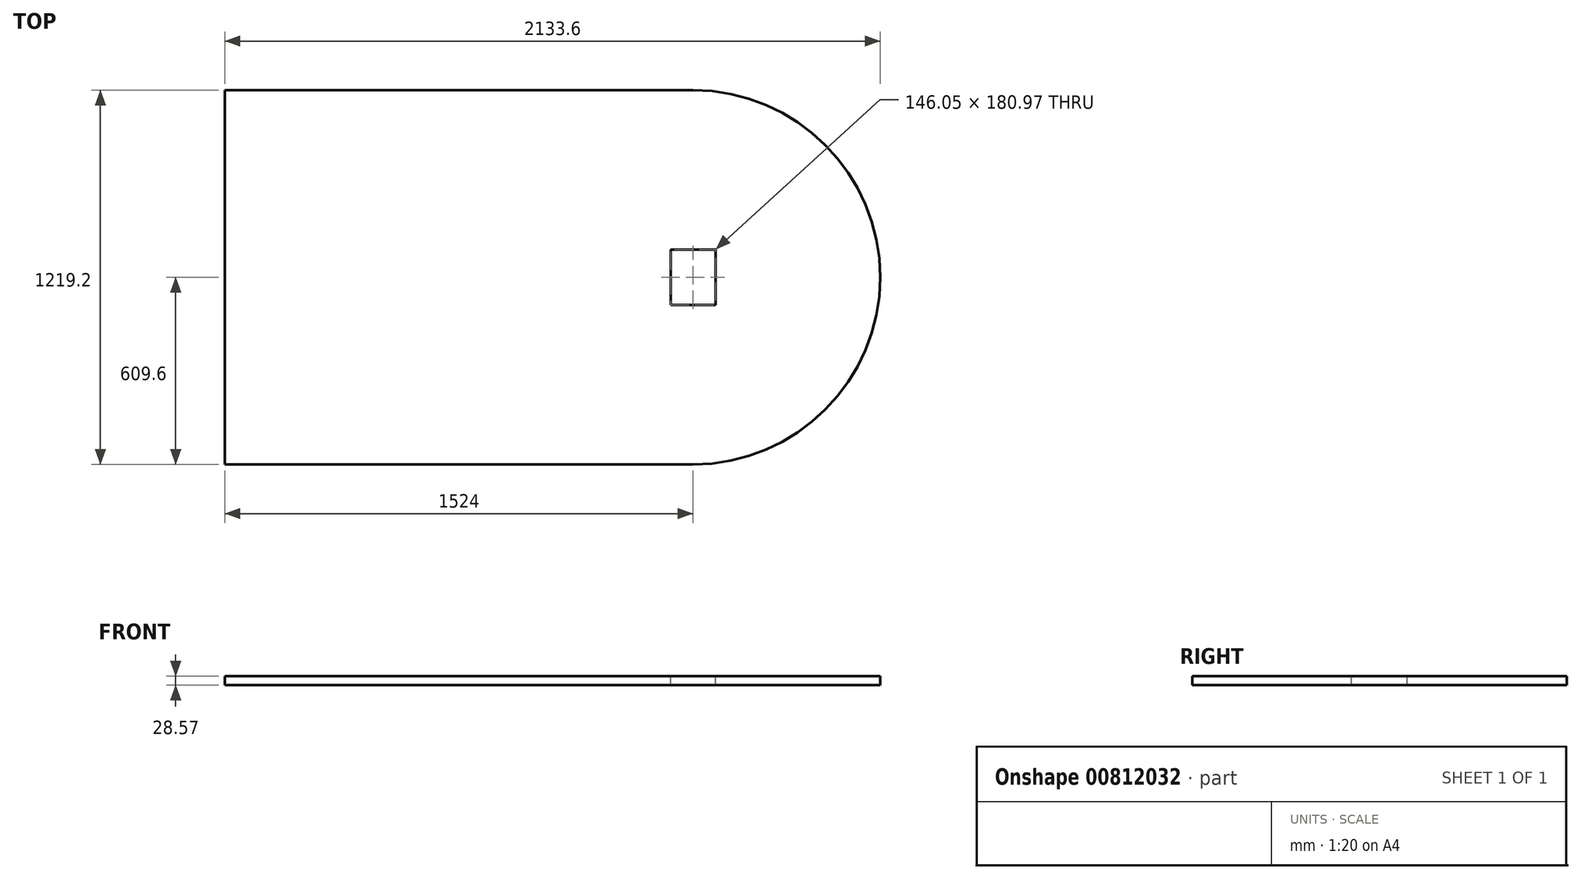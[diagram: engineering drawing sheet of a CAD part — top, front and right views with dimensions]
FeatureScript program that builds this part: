
annotation { "Feature Type Name" : "Feature", "Feature Type Description" : "" }
export const myFeature = defineFeature(function(context is Context, id is Id, definition is map)
    precondition{}
    {
        {
            var Q0;
            Q0=qCreatedBy(makeId("Top.planeOp"),FACE);
            var sketch = newSketch(context, id + "F0", { "sketchPlane" : qUnion([Q0])});
            skLineSegment(sketch, "E0.bottom", {"start": v(-762, 609.6) * mm, "end": v(762, 609.6) * mm});
            skLineSegment(sketch, "E0.top", {"start": v(-762, -609.6) * mm, "end": v(762, -609.6) * mm});
            skLineSegment(sketch, "E0.left", {"start": v(-762, 609.6) * mm, "end": v(-762, -609.6) * mm});
            skLineSegment(sketch, "E0.right", {"start": v(762, 609.6) * mm, "end": v(762, -609.6) * mm});
            skPoint(sketch, "E0.middle", {"position": v(0, 0) * mm});
            skArc(sketch, "E1", {"start": v(762, 609.6) * mm, "mid": v(1371.6, 0) * mm, "end": v(762, -609.6) * mm});
            skSolve(sketch);
        }
        {
            var Q0;
            Q0=makeQuery(id+"F0.imprint","IMPRINT",FACE,{"disambiguationData":[TD([[makeQuery(id+"F0.imprint","IMPRINT",EDGE,{"derivedFrom":sQuery(id+"F0.wireOp",EDGE,"E0.bottom")}),-1.0]])]});
            var Q1;
            Q1=makeQuery(id+"F0.imprint","IMPRINT",FACE,{"disambiguationData":[TD([[makeQuery(id+"F0.imprint","IMPRINT",EDGE,{"derivedFrom":sQuery(id+"F0.wireOp",EDGE,"E0.right")}),1.0]])]});
            extrude(context, id + "F1", {"entities" : qUnion([Q0, Q1]), "depth" : 28.57 * mm, "offsetDistance" : 25.4 * mm});
        }
        {
            var Q0;
            Q0=makeQuery(id+"F1.opExtrude","CAP_FACE",FACE,{"disambiguationData":[OSD([sQuery(id+"F0.wireOp",EDGE,"E0.bottom"),sQuery(id+"F0.wireOp",EDGE,"E0.top"),sQuery(id+"F0.wireOp",EDGE,"E0.left"),sQuery(id+"F0.wireOp",EDGE,"E1")])],"isStart":false});
            var sketch = newSketch(context, id + "F2", { "sketchPlane" : qUnion([Q0])});
            skLineSegment(sketch, "E2.bottom", {"start": v(835.03, 90.49) * mm, "end": v(688.98, 90.49) * mm});
            skLineSegment(sketch, "E2.top", {"start": v(835.03, -90.49) * mm, "end": v(688.98, -90.49) * mm});
            skLineSegment(sketch, "E2.left", {"start": v(835.03, 90.49) * mm, "end": v(835.03, -90.49) * mm});
            skLineSegment(sketch, "E2.right", {"start": v(688.98, 90.49) * mm, "end": v(688.98, -90.49) * mm});
            skPoint(sketch, "E2.middle", {"position": v(762, 0) * mm});
            skSolve(sketch);
        }
        {
            var Q0;
            Q0=makeQuery(id+"F2.imprint","IMPRINT",FACE,{"disambiguationData":[TD([[makeQuery(id+"F2.imprint","IMPRINT",EDGE,{"derivedFrom":sQuery(id+"F2.wireOp",EDGE,"E2.bottom")}),1.0]])]});
            extrude(context, id + "F3", {"entities" : qUnion([Q0]), "operationType" : NewBodyOperationType.REMOVE, "oppositeDirection" : true, "depth" : 50.8 * mm, "offsetDistance" : 25.4 * mm});
        }
    });
